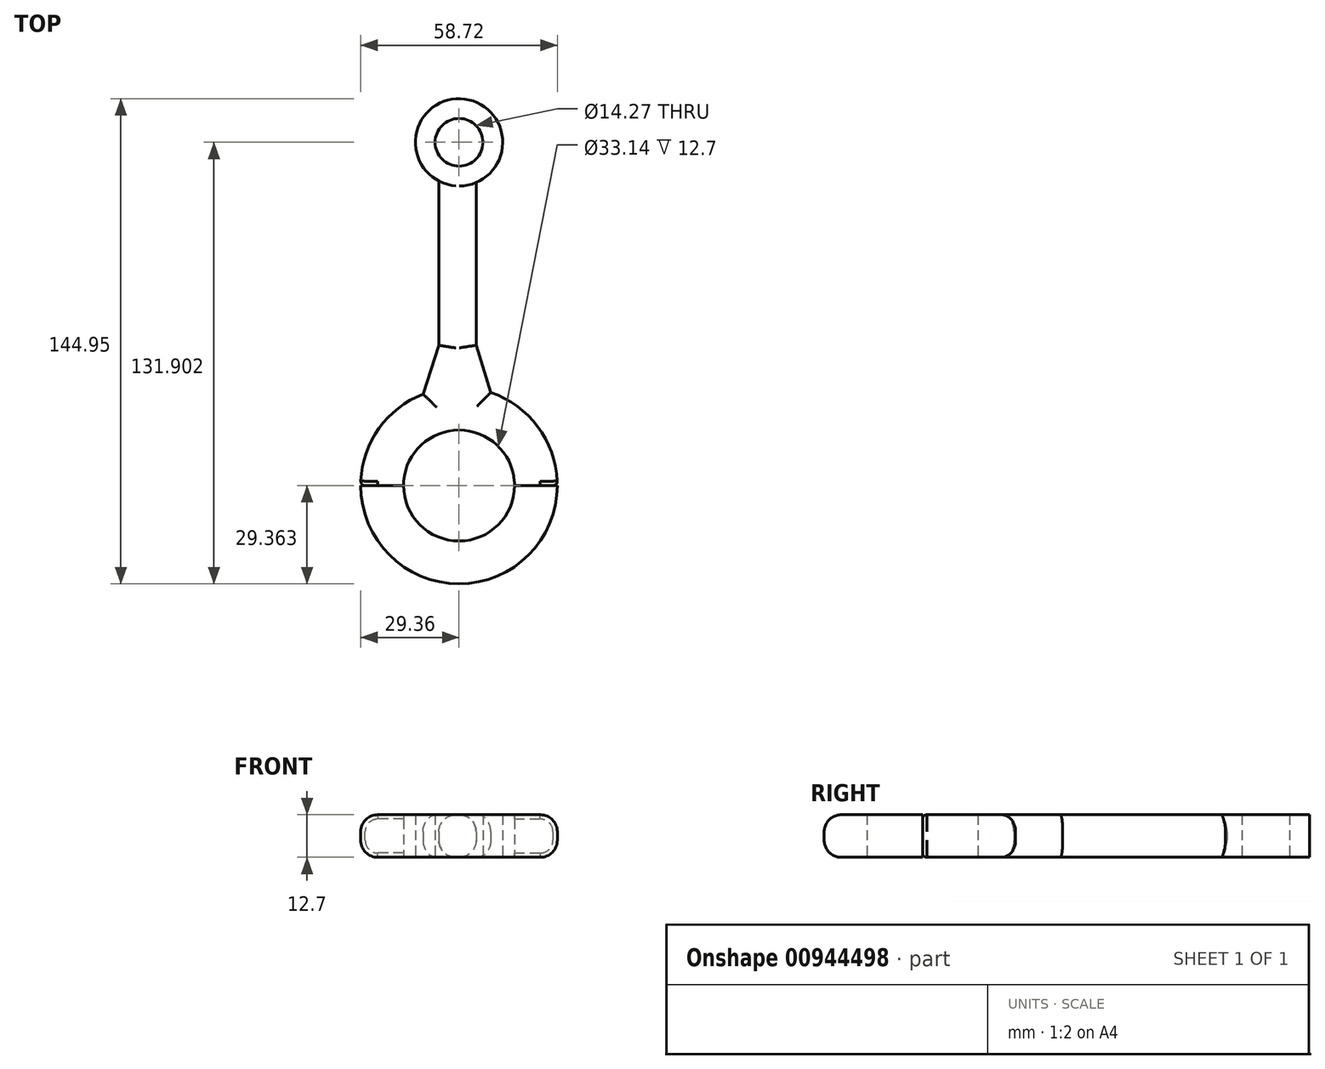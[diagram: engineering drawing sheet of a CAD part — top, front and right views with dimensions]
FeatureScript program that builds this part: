
annotation { "Feature Type Name" : "Feature", "Feature Type Description" : "" }
export const myFeature = defineFeature(function(context is Context, id is Id, definition is map)
    precondition{}
    {
        {
            var Q0;
            Q0=qCreatedBy(makeId("Top.planeOp"),FACE);
            var sketch = newSketch(context, id + "F0", { "sketchPlane" : qUnion([Q0])});
            skCircle(sketch, "E0", {"center": v(0, -54.17) * mm, "radius": 16.57 * mm});
            skCircle(sketch, "E1", {"center": v(0, 48.37) * mm, "radius": 7.14 * mm});
            skCircle(sketch, "E2", {"center": v(0, -54.17) * mm, "radius": 29.36 * mm});
            skCircle(sketch, "E3", {"center": v(0, 48.37) * mm, "radius": 13.05 * mm});
            skLineSegment(sketch, "E4", {"start": v(-6.01, 36.8) * mm, "end": v(-6.01, -12.26) * mm});
            skLineSegment(sketch, "E5", {"start": v(-6.01, -12.26) * mm, "end": v(-10.76, -26.85) * mm});
            skLineSegment(sketch, "E6", {"start": v(5.1, 36.37) * mm, "end": v(5.1, -12.26) * mm});
            skLineSegment(sketch, "E7", {"start": v(5.1, -12.26) * mm, "end": v(9.48, -26.38) * mm});
            skLineSegment(sketch, "E8", {"start": v(16.57, -54.17) * mm, "end": v(29.36, -54.17) * mm});
            skLineSegment(sketch, "E9", {"start": v(-16.57, -54.17) * mm, "end": v(-29.36, -54.17) * mm});
            skSolve(sketch);
        }
        {
            var Q0;
            {var subQ1=sQuery(id+"F0.wireOp",EDGE,"E4");Q0=makeQuery(id+"F0.imprint","IMPRINT",FACE,{"disambiguationData":[TD([[makeQuery(id+"F0.imprint","IMPRINT",EDGE,{"derivedFrom":subQ1}),1.0]])]});}
            var Q1;
            Q1=makeQuery(id+"F0.imprint","IMPRINT",FACE,{"disambiguationData":[TD([[makeQuery(id+"F0.imprint","IMPRINT",EDGE,{"derivedFrom":sQuery(id+"F0.wireOp",EDGE,"E1")}),-1.0]])]});
            extrude(context, id + "F1", {"entities" : qUnion([Q0, Q1]), "depth" : 12.7 * mm, "offsetDistance" : 25.4 * mm});
        }
        {
            var Q0;
            Q0=makeQuery(id+"F1.opExtrude","CAP_EDGE",EDGE,{"disambiguationData":[OSD([sQuery(id+"F0.wireOp",EDGE,"E6")])],"isStart":true});
            var Q1;
            Q1=makeQuery(id+"F1.opExtrude","CAP_EDGE",EDGE,{"disambiguationData":[OSD([sQuery(id+"F0.wireOp",EDGE,"E4")])],"isStart":true});
            var Q2;
            Q2=makeQuery(id+"F1.opExtrude","CAP_EDGE",EDGE,{"disambiguationData":[OSD([sQuery(id+"F0.wireOp",EDGE,"E4")])],"isStart":false});
            var Q3;
            Q3=makeQuery(id+"F1.opExtrude","CAP_EDGE",EDGE,{"disambiguationData":[OSD([sQuery(id+"F0.wireOp",EDGE,"E6")])],"isStart":false});
            var Q4;
            Q4=makeQuery(id+"F1.opExtrude","CAP_EDGE",EDGE,{"disambiguationData":[OSD([sQuery(id+"F0.wireOp",EDGE,"E5")])],"isStart":false});
            fillet(context, id + "F2", {"entities" : qUnion([Q0, Q1, Q2, Q3, Q4]), "radius" : 5.08 * mm, "tangentPropagation" : true, "allowEdgeOverflow" : false});
        }
        {
            var Q0;
            Q0=makeQuery(id+"F1.opExtrude","CAP_EDGE",EDGE,{"disambiguationData":[OSD([sQuery(id+"F0.wireOp",EDGE,"E7")])],"isStart":false});
            var Q1;
            Q1=makeQuery(id+"F1.opExtrude","CAP_EDGE",EDGE,{"disambiguationData":[OSD([sQuery(id+"F0.wireOp",EDGE,"E7")])],"isStart":true});
            var Q2;
            Q2=makeQuery(id+"F1.opExtrude","CAP_EDGE",EDGE,{"disambiguationData":[OSD([sQuery(id+"F0.wireOp",EDGE,"E5")])],"isStart":true});
            fillet(context, id + "F3", {"entities" : qUnion([Q0, Q1, Q2]), "radius" : 5.08 * mm, "tangentPropagation" : true, "allowEdgeOverflow" : false});
        }
        {
            var Q0;
            {var subQ3=sQuery(id+"F0.wireOp",EDGE,"E8");Q0=makeQuery(id+"F0.imprint","IMPRINT",FACE,{"disambiguationData":[TD([[makeQuery(id+"F0.imprint","IMPRINT",EDGE,{"derivedFrom":subQ3}),1.0]])]});}
            extrude(context, id + "F4", {"entities" : qUnion([Q0]), "operationType" : NewBodyOperationType.ADD, "depth" : 12.7 * mm, "offsetDistance" : 25.4 * mm});
        }
        {
            var Q0;
            {var subQ0=sQuery(id+"F0.wireOp",EDGE,"E2");var subQ1=sQuery(id+"F0.wireOp",EDGE,"E8");Q0=makeQuery(id+"F4.boolean.opBoolean","SPLIT",EDGE,{"disambiguationData":[TD([makeQuery(id+"F4.opExtrude","SWEPT_FACE",FACE,{"disambiguationData":[OSD([subQ1])]})])],"derivedFrom":makeQuery(id+"F4.opExtrude","CAP_EDGE",EDGE,{"disambiguationData":[OSD([subQ0])],"isStart":false})});}
            var Q1;
            {var subQ0=sQuery(id+"F0.wireOp",EDGE,"E8");var subQ1=sQuery(id+"F0.wireOp",EDGE,"E2");Q1=makeQuery(id+"F4.boolean.opBoolean","SPLIT",EDGE,{"disambiguationData":[TD([makeQuery(id+"F4.opExtrude","SWEPT_FACE",FACE,{"disambiguationData":[OSD([subQ0])]})])],"derivedFrom":makeQuery(id+"F4.opExtrude","CAP_EDGE",EDGE,{"disambiguationData":[OSD([subQ1])],"isStart":true})});}
            var Q2;
            {var subQ1=sQuery(id+"F0.wireOp",EDGE,"E2");var subQ2=sQuery(id+"F0.wireOp",EDGE,"E5");Q2=makeQuery(id+"F4.boolean.opBoolean","SPLIT",EDGE,{"disambiguationData":[TD([makeQuery(id+"F3.opFillet","BLEND_FACE",FACE,{"disambiguationData":[OSD([subQ2])]})])],"derivedFrom":makeQuery(id+"F4.opExtrude","CAP_EDGE",EDGE,{"disambiguationData":[OSD([subQ1])],"isStart":true})});}
            var Q3;
            {var subQ0=sQuery(id+"F0.wireOp",EDGE,"E2");var subQ2=sQuery(id+"F0.wireOp",EDGE,"E5");Q3=makeQuery(id+"F4.boolean.opBoolean","SPLIT",EDGE,{"disambiguationData":[TD([makeQuery(id+"F2.opFillet","BLEND_FACE",FACE,{"disambiguationData":[OSD([subQ2])]})])],"derivedFrom":makeQuery(id+"F4.opExtrude","CAP_EDGE",EDGE,{"disambiguationData":[OSD([subQ0])],"isStart":false})});}
            fillet(context, id + "F5", {"entities" : qUnion([Q0, Q1, Q2, Q3]), "radius" : 5.08 * mm, "tangentPropagation" : true, "allowEdgeOverflow" : false});
        }
        {
            var Q0;
            Q0=makeQuery(id+"F4.opExtrude","CAP_EDGE",EDGE,{"disambiguationData":[OSD([sQuery(id+"F0.wireOp",EDGE,"E9")])],"isStart":true});
            var Q1;
            Q1=makeQuery(id+"F4.opExtrude","CAP_EDGE",EDGE,{"disambiguationData":[OSD([sQuery(id+"F0.wireOp",EDGE,"E8")])],"isStart":true});
            var Q2;
            {var subQ0=sQuery(id+"F0.wireOp",EDGE,"E8");var subQ1=makeQuery(id+"F4.opExtrude","SWEPT_FACE",FACE,{"disambiguationData":[OSD([subQ0])]});var subQ2=sQuery(id+"F0.wireOp",EDGE,"E2");Q2=makeQuery(id+"F5.opFillet","BLEND_EDGE",EDGE,{"blendedFrom":[makeQuery(id+"F4.boolean.opBoolean","SPLIT",EDGE,{"disambiguationData":[TD([subQ1])],"derivedFrom":makeQuery(id+"F4.opExtrude","CAP_EDGE",EDGE,{"disambiguationData":[OSD([subQ2])],"isStart":true})}),subQ1],"blendedInto":[subQ1]});}
            fillet(context, id + "F6", {"entities" : qUnion([Q0, Q1, Q2]), "radius" : 1.27 * mm, "tangentPropagation" : true, "allowEdgeOverflow" : false});
        }
        {
            var Q0;
            {var subQ0=sQuery(id+"F0.wireOp",EDGE,"E8");Q0=makeQuery(id+"F0.imprint","IMPRINT",FACE,{"disambiguationData":[TD([[makeQuery(id+"F0.imprint","IMPRINT",EDGE,{"derivedFrom":subQ0}),-1.0]])]});}
            extrude(context, id + "F7", {"entities" : qUnion([Q0]), "operationType" : NewBodyOperationType.ADD, "depth" : 12.7 * mm, "offsetDistance" : 25.4 * mm});
        }
        {
            var Q0;
            Q0=makeQuery(id+"F7.opExtrude","CAP_EDGE",EDGE,{"disambiguationData":[OSD([sQuery(id+"F0.wireOp",EDGE,"E2")])],"isStart":true});
            fillet(context, id + "F8", {"entities" : qUnion([Q0]), "radius" : 5.08 * mm, "tangentPropagation" : true, "allowEdgeOverflow" : false});
        }
        {
            var Q0;
            Q0=makeQuery(id+"F7.opExtrude","CAP_EDGE",EDGE,{"disambiguationData":[OSD([sQuery(id+"F0.wireOp",EDGE,"E2")])],"isStart":false});
            fillet(context, id + "F9", {"entities" : qUnion([Q0]), "radius" : 5.08 * mm, "tangentPropagation" : true, "allowEdgeOverflow" : false});
        }
    });
